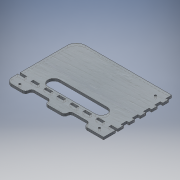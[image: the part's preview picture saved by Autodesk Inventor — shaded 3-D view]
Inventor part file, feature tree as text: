
AUTODESK INVENTOR PART (.ipt)
format: ipt  version: 2018.3 (Build 223284000, 284)  size: 218,112 bytes
history: native  units: mm
features: reference x12, other x4, extrude x3, sketch x3, fillet x2
ambient origin geometry x8: Origin, YZ Plane, XZ Plane, XY Plane, X Axis, Y Axis, Z Axis, Center Point
bodies: Solido1 (feature_tree)
feature tree (24):
  extrude  "Estrusione1"  Depth=80.0mm
  extrude  "Estrusione2"  Depth=4.0mm TaperAngle=0.0deg
  fillet  "Raccordo1"  Radius=4.0mm
  fillet  "Raccordo2"  Radius=15.0mm
  extrude  "Estrusione3"  Depth=10.0mm
  sketch  "Schizzo1"
  reference  "Riferimento14"
  reference  "Riferimento15"
  reference  "Riferimento16"
  reference  "Riferimento17"
  reference  "Riferimento18"
  reference  "Riferimento19"
  reference  "Riferimento20"
  reference  "Riferimento21"
  sketch  "Schizzo2"
  sketch  "Schizzo3"
  reference  "Riferimento22"
  reference  "Riferimento23"
  reference  "Riferimento24"
  reference  "Riferimento25"
  other  "<userpath>\Desktop\Scorbot Hardware\Case Board V2\caseHw v2.iam"
  other  "caseHw v2.iam"
  other  "tavolaBase:1"
  other  "Dietro:1"
